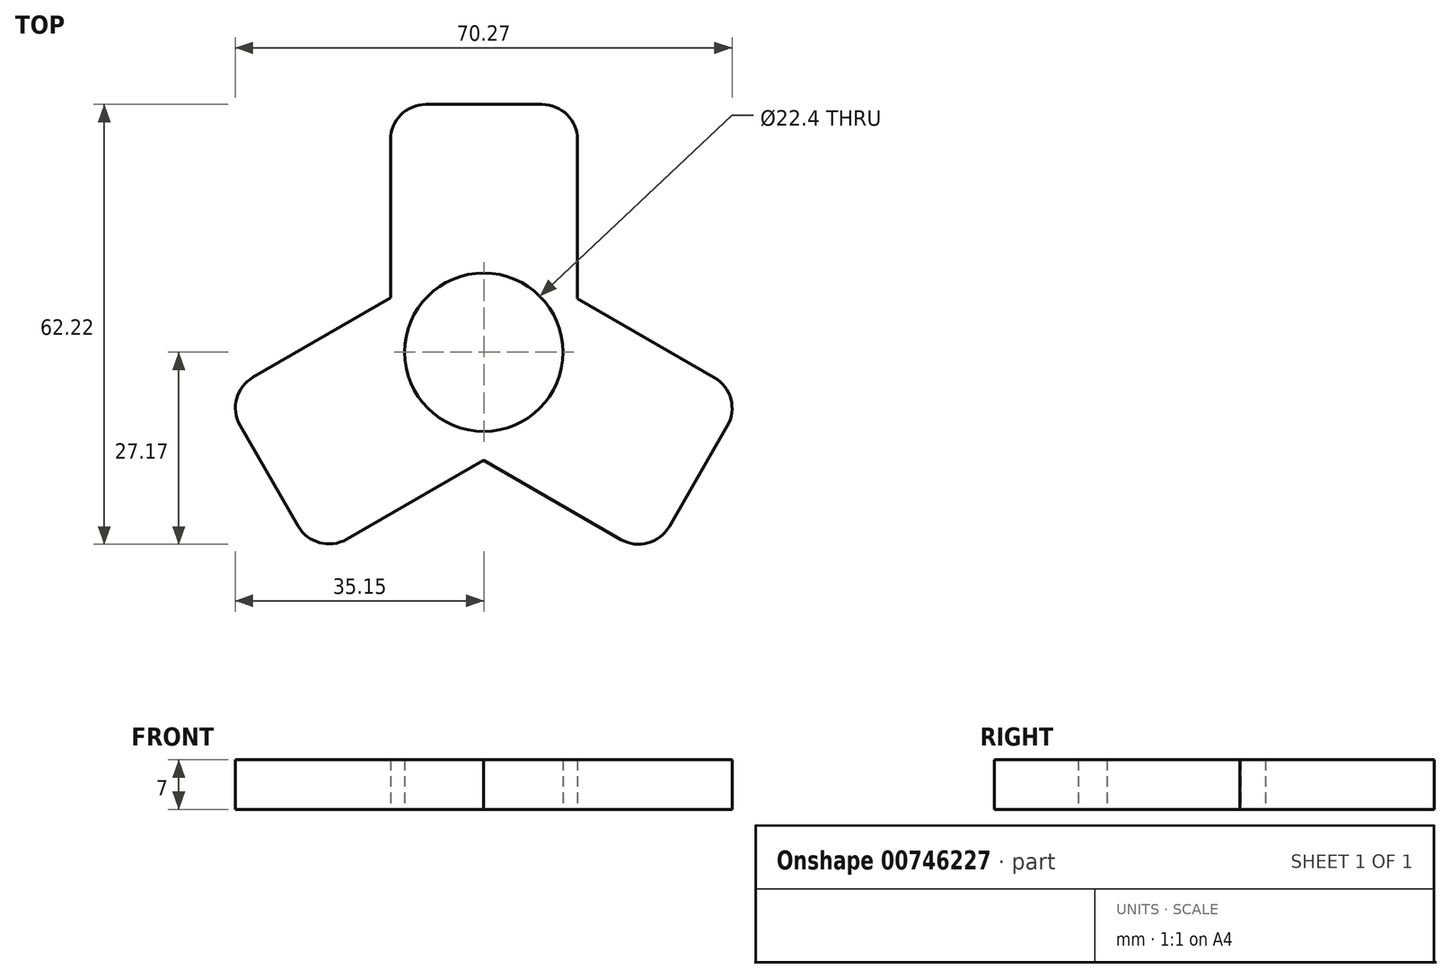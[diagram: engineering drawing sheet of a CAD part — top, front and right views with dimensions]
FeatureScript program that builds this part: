
annotation { "Feature Type Name" : "Feature", "Feature Type Description" : "" }
export const myFeature = defineFeature(function(context is Context, id is Id, definition is map)
    precondition{}
    {
        {
            var Q0;
            Q0=qCreatedBy(makeId("Top.planeOp"),FACE);
            var sketch = newSketch(context, id + "F0", { "sketchPlane" : qUnion([Q0])});
            skCircle(sketch, "E0", {"center": v(0, 0) * mm, "radius": 11.2 * mm});
            skLineSegment(sketch, "E1.bottom", {"start": v(-13.2, 0) * mm, "end": v(13.25, 0) * mm});
            skLineSegment(sketch, "E1.top", {"start": v(-13.2, 35.05) * mm, "end": v(13.25, 35.05) * mm});
            skLineSegment(sketch, "E1.left", {"start": v(-13.2, 7.68) * mm, "end": v(-13.2, 35.05) * mm});
            skLineSegment(sketch, "E1.right", {"start": v(13.25, 7.6) * mm, "end": v(13.25, 35.05) * mm});
            skLineSegment(sketch, "E2.1.0", {"start": v(-13.2, 7.68) * mm, "end": v(-36.98, -6.05) * mm});
            skLineSegment(sketch, "E2.1.1", {"start": v(-23.75, -28.96) * mm, "end": v(-36.98, -6.05) * mm});
            skLineSegment(sketch, "E2.1.2", {"start": v(-0.05, -15.27) * mm, "end": v(-23.75, -28.96) * mm});
            skLineSegment(sketch, "E2.2.0", {"start": v(-0.05, -15.27) * mm, "end": v(23.73, -29) * mm});
            skLineSegment(sketch, "E2.2.1", {"start": v(36.95, -6.1) * mm, "end": v(23.73, -29) * mm});
            skLineSegment(sketch, "E2.2.2", {"start": v(13.25, 7.6) * mm, "end": v(36.95, -6.1) * mm});
            skPoint(sketch, "E3.orphan", {"position": v(-6.62, 11.47) * mm});
            skPoint(sketch, "E4.orphan", {"position": v(6.6, 11.43) * mm});
            skPoint(sketch, "E5.orphan", {"position": v(6.6, -11.43) * mm});
            skPoint(sketch, "E6.orphan", {"position": v(-6.62, -11.47) * mm});
            skSolve(sketch);
        }
        {
            var Q0;
            Q0 = qSketchRegion(id + "F0", true);
            extrude(context, id + "F1", {"entities" : qUnion([Q0]), "depth" : 7 * mm, "offsetDistance" : 25 * mm});
        }
        {
            var Q0;
            Q0 = qSketchRegion(id + "F0", true);
            extrude(context, id + "F2", {"entities" : qUnion([Q0]), "operationType" : NewBodyOperationType.ADD, "depth" : 7 * mm, "offsetDistance" : 25 * mm});
        }
        {
            var Q0;
            Q0=makeQuery(id+"F1.opExtrude","SWEPT_EDGE",EDGE,{"disambiguationData":[OSD([sQuery(id+"F0.wireOp",EDGE,"E1.top"),sQuery(id+"F0.wireOp",EDGE,"E1.left")])]});
            var Q1;
            Q1=makeQuery(id+"F1.opExtrude","SWEPT_EDGE",EDGE,{"disambiguationData":[OSD([sQuery(id+"F0.wireOp",EDGE,"E1.top"),sQuery(id+"F0.wireOp",EDGE,"E1.right")])]});
            var Q2;
            Q2=makeQuery(id+"F1.opExtrude","SWEPT_EDGE",EDGE,{"disambiguationData":[OSD([sQuery(id+"F0.wireOp",EDGE,"E2.2.1"),sQuery(id+"F0.wireOp",EDGE,"E2.2.2")])]});
            var Q3;
            Q3=makeQuery(id+"F1.opExtrude","SWEPT_EDGE",EDGE,{"disambiguationData":[OSD([sQuery(id+"F0.wireOp",EDGE,"E2.2.0"),sQuery(id+"F0.wireOp",EDGE,"E2.2.1")])]});
            var Q4;
            Q4=makeQuery(id+"F1.opExtrude","SWEPT_EDGE",EDGE,{"disambiguationData":[OSD([sQuery(id+"F0.wireOp",EDGE,"E2.1.1"),sQuery(id+"F0.wireOp",EDGE,"E2.1.2")])]});
            var Q5;
            Q5=makeQuery(id+"F1.opExtrude","SWEPT_EDGE",EDGE,{"disambiguationData":[OSD([sQuery(id+"F0.wireOp",EDGE,"E2.1.0"),sQuery(id+"F0.wireOp",EDGE,"E2.1.1")])]});
            fillet(context, id + "F3", {"entities" : qUnion([Q0, Q1, Q2, Q3, Q4, Q5]), "radius" : 5 * mm, "tangentPropagation" : true, "allowEdgeOverflow" : false});
        }
    });
